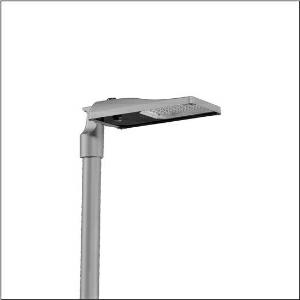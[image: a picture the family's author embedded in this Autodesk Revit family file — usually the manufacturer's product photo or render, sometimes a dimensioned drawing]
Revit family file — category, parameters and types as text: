
# Revit family: streetlight_sl_31_mini___st1_0a_5xh2d71t08ga_b82e
name_source: partatom
category: Lighting Fixtures
units: mm (PartAtom-declared; Revit-internal decimal feet)

## family parameters
Cut with Voids When Loaded = No
Host = Face
Light Source = No
Part Type = Normal
Room Calculation Point = No
Round Connector Dimension = Use Diameter
Shared = No

## types (1)
- --- (1 x LED, 4860 lm, 39.3 W, 2200K)
    Apparent Load = 39 VA
    CIE Flux Codes = 37 72 97 100 100
    Color Rendering = 70
    Color Temperature = 2200K
    Default Elevation = 1800 mm
    Description = Streetlight SL 31 mini D4i, Desk-Remote mast luminaire for post-top, side-entry; light control with lens of PMMA; light distribution: ST1.0a, direct asymmetric distribution, for standard-compliant lighting for roads and squares; LED: luminous flux: 4.860lm, light colour: 722, colour temperature: 2200K; luminous efficacy: 123,7lm/W; control: pre-setting: logarithmic dimming characteristic, flexible luminous flux parameterisation, time-dependent luminous flux control, constant luminous flux control, power reduction, intelligent temperature release in ECG and LED module, overheat protection; luminaire housing, of diecast aluminium, Siteco® metallic grey (DB 702S), corrosivity category C5 high according to DIN EN ISO 12944; cover of toughened safety glass, transparent, mast flange of diecast aluminium, Siteco® metallic grey (DB 702S), spigot size: 76/60mm, mast flange included unmounted; with cable H07RN-F 2x 1.5mm², cable length: 6,5m, connection cable pre-assembled; mains connection: 220..240V, AC, 50/60Hz; power consumption (at start of service life): 39,3W / (at end of service life): 40,7W / (with reduced operation 50%): 18,1W; protection rating (complete): IP66; insulation class (complete): insulation class II (safety insulation); impact resistance: IK09; certification: CE, ENEC, ENEC+, VDE, UKCA, ZD4i; permissible operating ambient temperature for outdoor applications: -40..+50°C; packaging unit: 1 piece

Light Distribution: ST1.0a
    Height = 76 mm
    Lamp = 1 x LED
    Lamp Light Flux = 4860 lm
    Lamp Power = 39.3 W
    Lamp count = 1
    Length = 547 mm
    Luminous efficacy = 124 lm/W
    Manufacturer = Siteco
    ModVariant = No
    Model = 5XH2D71T08GA
    Number of Poles = 1
    OnlyDefault = Yes
    Power Factor = 1
    Product Name = Streetlight SL 31 mini | ST1.0a
    Product group = mast luminaire | pylon top
    ProductGroupID = 6100
    Protection Class = Protection class II
    Protection Degree = IP 66
    RLX_Detail_Level = 1
    RLX_Emergency_Light_Flux = 0 lm
    RLX_Emergency_Type = 0
    RLX_Emergency_Type_DB = No
    RlxData = <blob elided: 39681 chars, md5=2e04a7a0>
    Socket = socket
    Standby Power = 0 W
    System Light Flux = 4860 lm
    System Power = 39 W
    Type Comments = factory setting: luminous flux: 100 % | dim-lin: 254 | 798 mA
    Type Image = l_1300332.jpg
    URL = http://relux.com
    VarID = @adj_054704
    Voltage = 0 V
    Weight = 0.00 kg
    Width = 265 mm

## geometry (parser evidence)
native form markers: Blend x4, Sweep x9
no freeform markers — native parametric forms only
